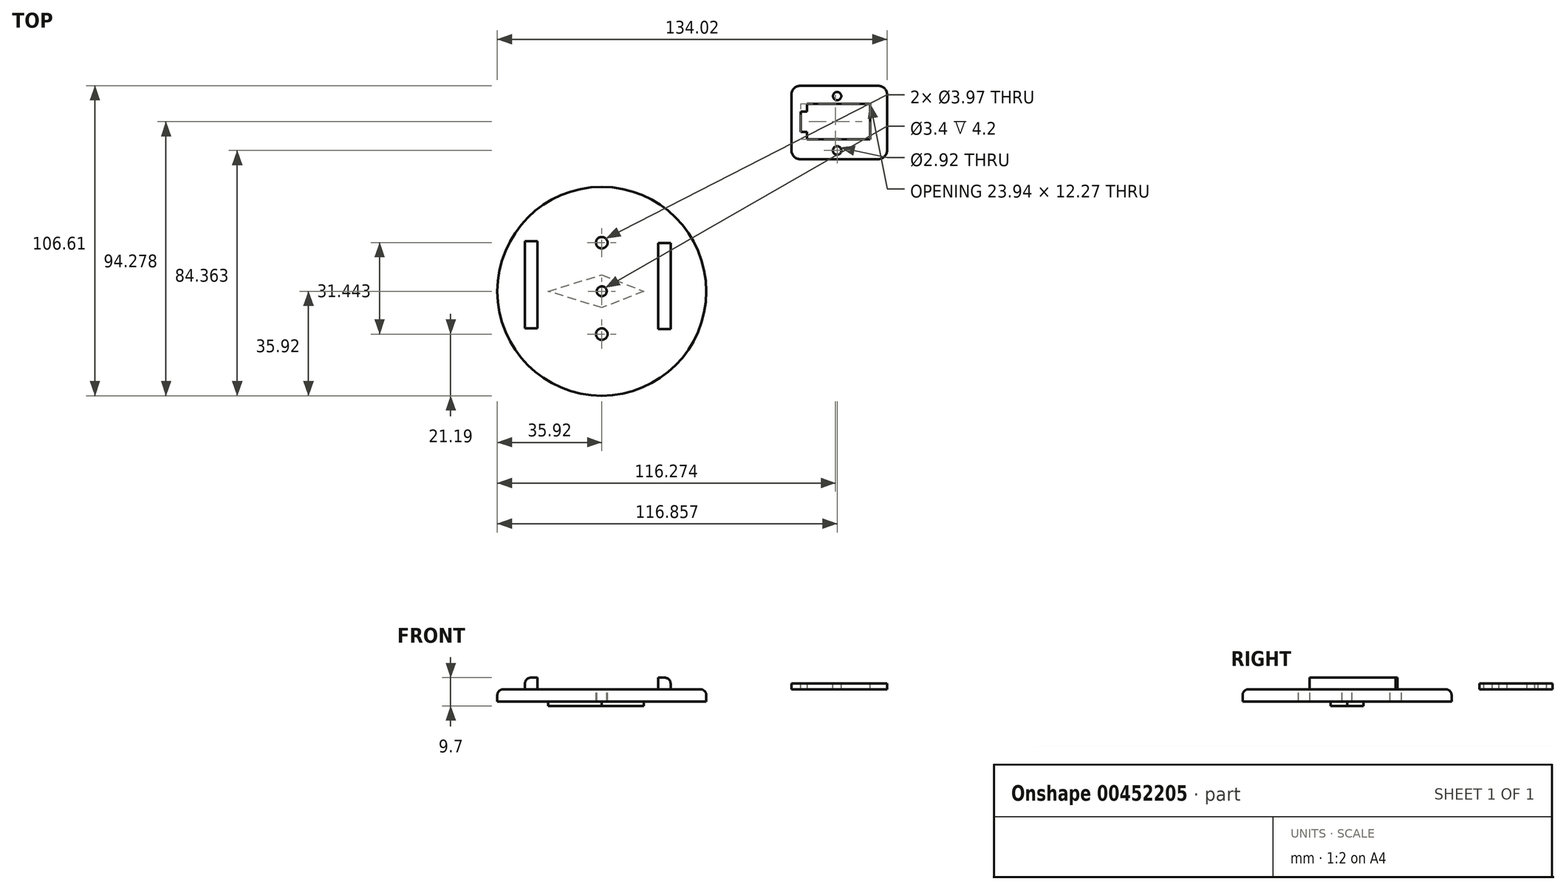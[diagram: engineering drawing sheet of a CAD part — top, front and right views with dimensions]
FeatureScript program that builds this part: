
annotation { "Feature Type Name" : "Feature", "Feature Type Description" : "" }
export const myFeature = defineFeature(function(context is Context, id is Id, definition is map)
    precondition{}
    {
        {
            var Q0;
            Q0=qCreatedBy(makeId("Top.planeOp"),FACE);
            var sketch = newSketch(context, id + "F0", { "sketchPlane" : qUnion([Q0])});
            skCircle(sketch, "E0", {"center": v(0, 0) * mm, "radius": 35.92 * mm});
            skSolve(sketch);
        }
        {
            var Q0;
            Q0=makeQuery(id+"F0.imprint","IMPRINT",FACE,{"disambiguationData":[TD([[makeQuery(id+"F0.imprint","IMPRINT",EDGE,{"derivedFrom":sQuery(id+"F0.wireOp",EDGE,"E0")}),1.0]])]});
            extrude(context, id + "F1", {"entities" : qUnion([Q0]), "oppositeDirection" : true, "depth" : 4.2 * mm});
        }
        {
            var Q0;
            Q0=makeQuery(id+"F1.opExtrude","CAP_FACE",FACE,{"disambiguationData":[OSD([sQuery(id+"F0.wireOp",EDGE,"E0")])],"isStart":true});
            fillet(context, id + "F2", {"entities" : qUnion([Q0]), "radius" : 2 * mm, "tangentPropagation" : true, "allowEdgeOverflow" : false});
        }
        {
            var Q0;
            Q0=makeQuery(id+"F1.opExtrude","CAP_FACE",FACE,{"disambiguationData":[OSD([sQuery(id+"F0.wireOp",EDGE,"E0")])],"isStart":true});
            var sketch = newSketch(context, id + "F3", { "sketchPlane" : qUnion([Q0])});
            skCircle(sketch, "E1", {"center": v(0, 0) * mm, "radius": 1.7 * mm});
            skSolve(sketch);
        }
        {
            var Q0;
            Q0=makeQuery(id+"F3.imprint","IMPRINT",FACE,{"disambiguationData":[TD([[makeQuery(id+"F3.imprint","IMPRINT",EDGE,{"derivedFrom":sQuery(id+"F3.wireOp",EDGE,"E1")}),-1.0]])]});
            var sketch = newSketch(context, id + "F4", { "sketchPlane" : qUnion([Q0])});
            skLineSegment(sketch, "E2", {"start": v(0, 16.71) * mm, "end": v(0, -15.01) * mm});
            skSolve(sketch);
        }
        {
            var Q0;
            Q0=makeQuery(id+"F3.imprint","IMPRINT",FACE,{"disambiguationData":[TD([[makeQuery(id+"F3.imprint","IMPRINT",EDGE,{"derivedFrom":sQuery(id+"F3.wireOp",EDGE,"E1")}),-1.0]])]});
            var sketch = newSketch(context, id + "F5", { "sketchPlane" : qUnion([Q0])});
            skCircle(sketch, "E3", {"center": v(0, 16.71) * mm, "radius": 1.98 * mm});
            skCircle(sketch, "E4", {"center": v(0, -14.73) * mm, "radius": 1.98 * mm});
            skSolve(sketch);
        }
        {
            var Q0;
            Q0=makeQuery(id+"F3.imprint","IMPRINT",FACE,{"disambiguationData":[TD([[makeQuery(id+"F3.imprint","IMPRINT",EDGE,{"derivedFrom":sQuery(id+"F3.wireOp",EDGE,"E1")}),1.0]])]});
            var Q1;
            Q1 = qSketchRegion(id + "F5", true);
            extrude(context, id + "F6", {"entities" : qUnion([Q0, Q1]), "operationType" : NewBodyOperationType.REMOVE, "oppositeDirection" : true, "depth" : 25 * mm});
        }
        {
            var Q0;
            {var subQ0=sQuery(id+"F0.wireOp",EDGE,"E0");Q0=makeQuery(id+"F4.imprint","IMPRINT",FACE,{"disambiguationData":[TD([[makeQuery(id+"F4.imprint","IMPRINT",EDGE,{"derivedFrom":makeQuery(id+"F3.imprint","IMPRINT",EDGE,{"derivedFrom":makeQuery(id+"F2.opFillet","BLEND_EDGE",EDGE,{"blendedFrom":[makeQuery(id+"F1.opExtrude","CAP_EDGE",EDGE,{"disambiguationData":[OSD([subQ0])],"isStart":true}),makeQuery(id+"F1.opExtrude","CAP_FACE",FACE,{"disambiguationData":[OSD([subQ0])],"isStart":true})],"blendedInto":[makeQuery(id+"F1.opExtrude","CAP_FACE",FACE,{"disambiguationData":[OSD([subQ0])],"isStart":true})]})})}),1.0]])]});}
            var sketch = newSketch(context, id + "F7", { "sketchPlane" : qUnion([Q0])});
            skLineSegment(sketch, "E5.bottom", {"start": v(19.41, 16.65) * mm, "end": v(23.66, 16.65) * mm});
            skLineSegment(sketch, "E5.top", {"start": v(19.41, -12.95) * mm, "end": v(23.66, -12.95) * mm});
            skLineSegment(sketch, "E5.left", {"start": v(19.41, 16.65) * mm, "end": v(19.41, -12.95) * mm});
            skLineSegment(sketch, "E5.right", {"start": v(23.66, 16.65) * mm, "end": v(23.66, -12.95) * mm});
            skSolve(sketch);
        }
        {
            var Q0;
            {var subQ0=sQuery(id+"F0.wireOp",EDGE,"E0");Q0=makeQuery(id+"F4.imprint","IMPRINT",FACE,{"disambiguationData":[TD([[makeQuery(id+"F4.imprint","IMPRINT",EDGE,{"derivedFrom":makeQuery(id+"F3.imprint","IMPRINT",EDGE,{"derivedFrom":makeQuery(id+"F2.opFillet","BLEND_EDGE",EDGE,{"blendedFrom":[makeQuery(id+"F1.opExtrude","CAP_EDGE",EDGE,{"disambiguationData":[OSD([subQ0])],"isStart":true}),makeQuery(id+"F1.opExtrude","CAP_FACE",FACE,{"disambiguationData":[OSD([subQ0])],"isStart":true})],"blendedInto":[makeQuery(id+"F1.opExtrude","CAP_FACE",FACE,{"disambiguationData":[OSD([subQ0])],"isStart":true})]})})}),1.0]])]});}
            var sketch = newSketch(context, id + "F8", { "sketchPlane" : qUnion([Q0])});
            skLineSegment(sketch, "E6.bottom", {"start": v(-26.4, 17.28) * mm, "end": v(-22.12, 17.28) * mm});
            skLineSegment(sketch, "E6.top", {"start": v(-26.4, -12.74) * mm, "end": v(-22.12, -12.74) * mm});
            skLineSegment(sketch, "E6.left", {"start": v(-26.4, 17.28) * mm, "end": v(-26.4, -12.74) * mm});
            skLineSegment(sketch, "E6.right", {"start": v(-22.12, 17.28) * mm, "end": v(-22.12, -12.74) * mm});
            skSolve(sketch);
        }
        {
            var Q0;
            Q0 = qSketchRegion(id + "F8", true);
            var Q1;
            Q1 = qSketchRegion(id + "F7", true);
            extrude(context, id + "F9", {"entities" : qUnion([Q0, Q1]), "operationType" : NewBodyOperationType.ADD, "depth" : 4 * mm});
        }
        {
            var Q0;
            Q0=makeQuery(id+"F9.opExtrude","CAP_EDGE",EDGE,{"disambiguationData":[OSD([sQuery(id+"F8.wireOp",EDGE,"E6.left")])],"isStart":false});
            fillet(context, id + "F10", {"entities" : qUnion([Q0]), "radius" : 2 * mm, "tangentPropagation" : true, "allowEdgeOverflow" : false});
        }
        {
            var Q0;
            Q0=makeQuery(id+"F9.opExtrude","CAP_EDGE",EDGE,{"disambiguationData":[OSD([sQuery(id+"F7.wireOp",EDGE,"E5.right")])],"isStart":false});
            fillet(context, id + "F11", {"entities" : qUnion([Q0]), "radius" : 2 * mm, "tangentPropagation" : true, "allowEdgeOverflow" : false});
        }
        {
            var Q0;
            Q0=makeQuery(id+"F1.opExtrude","CAP_FACE",FACE,{"disambiguationData":[OSD([sQuery(id+"F0.wireOp",EDGE,"E0")])],"isStart":false});
            var sketch = newSketch(context, id + "F12", { "sketchPlane" : qUnion([Q0])});
            skLineSegment(sketch, "E7", {"start": v(-18.13, 0) * mm, "end": v(14.16, 0) * mm});
            skSolve(sketch);
        }
        {
            var Q0;
            {var subQ1=sQuery(id+"F0.wireOp",EDGE,"E0");Q0=makeQuery(id+"F12.imprint","IMPRINT",FACE,{"disambiguationData":[TD([[makeQuery(id+"F12.imprint","IMPRINT",EDGE,{"derivedFrom":makeQuery(id+"F1.opExtrude","CAP_EDGE",EDGE,{"disambiguationData":[OSD([subQ1])],"isStart":false})}),-1.0]])]});}
            var sketch = newSketch(context, id + "F13", { "sketchPlane" : qUnion([Q0])});
            skLineSegment(sketch, "E8", {"start": v(-18.41, 0) * mm, "end": v(0, -5.67) * mm});
            skLineSegment(sketch, "E9", {"start": v(0, -5.67) * mm, "end": v(14.45, 0) * mm});
            skLineSegment(sketch, "E10", {"start": v(14.45, 0) * mm, "end": v(0, 5.67) * mm});
            skLineSegment(sketch, "E11", {"start": v(0, 5.67) * mm, "end": v(-18.41, 0) * mm});
            skSolve(sketch);
        }
        {
            var Q0;
            Q0 = qSketchRegion(id + "F13", true);
            extrude(context, id + "F14", {"entities" : qUnion([Q0]), "operationType" : NewBodyOperationType.ADD, "depth" : 1.5 * mm});
        }
        {
            var Q0;
            Q0=qCreatedBy(makeId("Top.planeOp"),FACE);
            var sketch = newSketch(context, id + "F15", { "sketchPlane" : qUnion([Q0])});
            skLineSegment(sketch, "E12.bottom", {"start": v(65.25, 70.7) * mm, "end": v(98.1, 70.7) * mm});
            skLineSegment(sketch, "E12.top", {"start": v(65.25, 45.45) * mm, "end": v(98.1, 45.45) * mm});
            skLineSegment(sketch, "E12.left", {"start": v(65.25, 70.7) * mm, "end": v(65.25, 45.45) * mm});
            skLineSegment(sketch, "E12.right", {"start": v(98.1, 70.7) * mm, "end": v(98.1, 45.45) * mm});
            skSolve(sketch);
        }
        {
            var Q0;
            Q0=makeQuery(id+"F15.imprint","IMPRINT",FACE,{"disambiguationData":[TD([[makeQuery(id+"F15.imprint","IMPRINT",EDGE,{"derivedFrom":sQuery(id+"F15.wireOp",EDGE,"E12.bottom")}),-1.0]])]});
            extrude(context, id + "F16", {"entities" : qUnion([Q0]), "depth" : 2 * mm});
        }
        {
            var Q0;
            Q0=makeQuery(id+"F16.opExtrude","SWEPT_EDGE",EDGE,{"disambiguationData":[OSD([sQuery(id+"F15.wireOp",EDGE,"E12.bottom"),sQuery(id+"F15.wireOp",EDGE,"E12.left")])]});
            var Q1;
            Q1=makeQuery(id+"F16.opExtrude","SWEPT_EDGE",EDGE,{"disambiguationData":[OSD([sQuery(id+"F15.wireOp",EDGE,"E12.top"),sQuery(id+"F15.wireOp",EDGE,"E12.right")])]});
            var Q2;
            Q2=makeQuery(id+"F16.opExtrude","SWEPT_EDGE",EDGE,{"disambiguationData":[OSD([sQuery(id+"F15.wireOp",EDGE,"E12.bottom"),sQuery(id+"F15.wireOp",EDGE,"E12.right")])]});
            var Q3;
            Q3=makeQuery(id+"F16.opExtrude","SWEPT_EDGE",EDGE,{"disambiguationData":[OSD([sQuery(id+"F15.wireOp",EDGE,"E12.top"),sQuery(id+"F15.wireOp",EDGE,"E12.left")])]});
            fillet(context, id + "F17", {"entities" : qUnion([Q0, Q1, Q2, Q3]), "radius" : 3 * mm, "tangentPropagation" : true, "allowEdgeOverflow" : false});
        }
        {
            var Q0;
            Q0=makeQuery(id+"F16.opExtrude","CAP_FACE",FACE,{"disambiguationData":[OSD([sQuery(id+"F15.wireOp",EDGE,"E12.bottom"),sQuery(id+"F15.wireOp",EDGE,"E12.top"),sQuery(id+"F15.wireOp",EDGE,"E12.left"),sQuery(id+"F15.wireOp",EDGE,"E12.right")])],"isStart":false});
            var sketch = newSketch(context, id + "F18", { "sketchPlane" : qUnion([Q0])});
            skLineSegment(sketch, "E13", {"start": v(65.25, 57.23) * mm, "end": v(70.17, 57.23) * mm});
            skSolve(sketch);
        }
        {
            var Q0;
            {var subQ3=sQuery(id+"F15.wireOp",EDGE,"E12.bottom");Q0=makeQuery(id+"F18.imprint","IMPRINT",FACE,{"disambiguationData":[TD([[makeQuery(id+"F18.imprint","IMPRINT",EDGE,{"derivedFrom":makeQuery(id+"F16.opExtrude","CAP_EDGE",EDGE,{"disambiguationData":[OSD([subQ3])],"isStart":false})}),-1.0]])]});}
            var sketch = newSketch(context, id + "F19", { "sketchPlane" : qUnion([Q0])});
            skLineSegment(sketch, "E14.bottom", {"start": v(70.53, 64.5) * mm, "end": v(92.32, 64.5) * mm});
            skLineSegment(sketch, "E14.top", {"start": v(70.53, 52.22) * mm, "end": v(92.32, 52.22) * mm});
            skLineSegment(sketch, "E14.left", {"start": v(70.53, 64.5) * mm, "end": v(70.53, 52.22) * mm});
            skLineSegment(sketch, "E14.right", {"start": v(92.32, 64.5) * mm, "end": v(92.32, 52.22) * mm});
            skSolve(sketch);
        }
        {
            var Q0;
            {var subQ3=sQuery(id+"F15.wireOp",EDGE,"E12.bottom");Q0=makeQuery(id+"F18.imprint","IMPRINT",FACE,{"disambiguationData":[TD([[makeQuery(id+"F18.imprint","IMPRINT",EDGE,{"derivedFrom":makeQuery(id+"F16.opExtrude","CAP_EDGE",EDGE,{"disambiguationData":[OSD([subQ3])],"isStart":false})}),-1.0]])]});}
            var sketch = newSketch(context, id + "F20", { "sketchPlane" : qUnion([Q0])});
            skLineSegment(sketch, "E15.bottom", {"start": v(71.6, 61.75) * mm, "end": v(68.38, 61.75) * mm});
            skLineSegment(sketch, "E15.top", {"start": v(71.6, 54.84) * mm, "end": v(68.38, 54.84) * mm});
            skLineSegment(sketch, "E15.left", {"start": v(71.6, 61.75) * mm, "end": v(71.6, 54.84) * mm});
            skLineSegment(sketch, "E15.right", {"start": v(68.38, 61.75) * mm, "end": v(68.38, 54.84) * mm});
            skSolve(sketch);
        }
        {
            var Q0;
            Q0=makeQuery(id+"F19.imprint","IMPRINT",FACE,{"disambiguationData":[TD([[makeQuery(id+"F19.imprint","IMPRINT",EDGE,{"derivedFrom":sQuery(id+"F19.wireOp",EDGE,"E14.bottom")}),-1.0]])]});
            var Q1;
            Q1=makeQuery(id+"F20.imprint","IMPRINT",FACE,{"disambiguationData":[TD([[makeQuery(id+"F20.imprint","IMPRINT",EDGE,{"derivedFrom":sQuery(id+"F20.wireOp",EDGE,"E15.bottom")}),1.0]])]});
            extrude(context, id + "F21", {"entities" : qUnion([Q0, Q1]), "operationType" : NewBodyOperationType.REMOVE, "oppositeDirection" : true, "depth" : 25 * mm});
        }
        {
            var Q0;
            {var subQ3=sQuery(id+"F15.wireOp",EDGE,"E12.bottom");Q0=makeQuery(id+"F18.imprint","IMPRINT",FACE,{"disambiguationData":[TD([[makeQuery(id+"F18.imprint","IMPRINT",EDGE,{"derivedFrom":makeQuery(id+"F16.opExtrude","CAP_EDGE",EDGE,{"disambiguationData":[OSD([subQ3])],"isStart":false})}),-1.0]])]});}
            var sketch = newSketch(context, id + "F22", { "sketchPlane" : qUnion([Q0])});
            skCircle(sketch, "E16", {"center": v(80.94, 67.14) * mm, "radius": 1.42 * mm});
            skCircle(sketch, "E17", {"center": v(80.94, 48.44) * mm, "radius": 1.46 * mm});
            skSolve(sketch);
        }
        {
            var Q0;
            Q0 = qSketchRegion(id + "F22", true);
            extrude(context, id + "F23", {"entities" : qUnion([Q0]), "operationType" : NewBodyOperationType.REMOVE, "oppositeDirection" : true, "depth" : 25 * mm});
        }
    });
